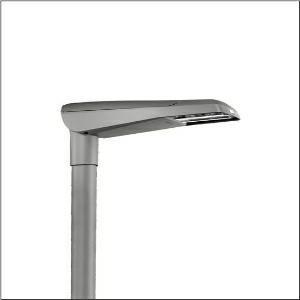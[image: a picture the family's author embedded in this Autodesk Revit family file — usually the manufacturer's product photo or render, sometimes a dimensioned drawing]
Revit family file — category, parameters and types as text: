
# Revit family: streetlight_sl_11_iq_micro___st0_5a_5xc1bc1f08ce_e478
name_source: partatom
category: Lighting Fixtures
units: mm (PartAtom-declared; Revit-internal decimal feet)

## family parameters
Cut with Voids When Loaded = No
Host = Face
Light Source = No
Part Type = Normal
Room Calculation Point = No
Round Connector Dimension = Use Diameter
Shared = No

## types (1)
- --- (1 x LED, 1580 lm, 14 W, 2200K)
    Apparent Load = 14 VA
    CIE Flux Codes = 42 72 97 100 100
    Color Rendering = 70
    Color Temperature = 2200K
    Default Elevation = 1800 mm
    Description = Streetlight SL 11 iQ micro, mast luminaire, primary light control with 3 zone facetted reflector, of plastic, silver coated, highly specular, primary optical cover: cover, of PMMA, transparent, light distribution: ST0.5a, light emission: direct distribution, primary light characteristic: asymmetric, installation type: post-top, side-entry, lamps: LED, High Power LED, rated values: 1.860lm | 13,8W | 134,8lm/W (begin service life); end service life: 1.860lm | 14W; at 50% lumin. flux: 930lm | 7,5W | 124lm/W, colour temperature: 2200/2700/3000/4000K, colour rendering: CRI > 70, light colour: 722/727/730/740, light setting 1 begin service life: 100% | 1.860lm | 13,8W | 134,8lm/W | 3.000K, light setting 1 end service life: 14W, further light settings possible, control: Street-Remote, Auto-Match, Temp-Guard, Lumen-Switch, Night-Set, Smart-Wire, Light-Fading, Desk-Remote (wireless, voltage-free reading and setting of iQ features in the workshop via application-optimized NFC function/RFID function), optimised constant luminous flux control (CLO 2.0), with cable H07RN-F 5x 1.5mm², mains connection: 220..240V, AC, 50/60Hz, connection cable pre-assembled, cable length: 5,5m, luminaire housing, of diecast aluminium, powder-coated, Siteco® metallic grey (DB 702S), please order mast flange separately, inclination adjustable without tools: 0°, 5°, 10°, 15° (post-top) | 0°, -5°, -10°, -15° (side-entry), sealing non-destructively replaceable, multi-level sealing system, length: 600mm, width: 174mm, height: 116mm, mast flange for spigot size: 42mm (side-entry): 5XC10008XM4, 60/48mm (side-entry/post-top): 5XC10108XM2, 76/60mm (side-entry/post-top): 5XC10108XM1, equipment: standard, protection rating (complete): IP66, insulation class (complete): insulation class II (safety insulation), certification: CE, ENEC, ENEC+, VDE, impact resistance: IK10, permissible operating ambient temperature for outdoor applications: -25..+50°C, standard-compliant lighting for roads and squares, Environmental Product Declaration (EPD) tested and certified by an independent institute, packaging unit: 1 piece

Light Distribution: ST0.5a
    Height = 116 mm
    Lamp = 1 x LED
    Lamp Light Flux = 1580 lm
    Lamp Power = 14 W
    Lamp count = 1
    Length = 600 mm
    Luminous efficacy = 113 lm/W
    Manufacturer = Siteco
    ModVariant = No
    Model = 5XC1BC1F08CE
    Number of Poles = 1
    OnlyDefault = Yes
    Power Factor = 1
    Product Name = Streetlight SL 11 iQ micro | ST0.5a
    Product group = mast luminaire | pylon top
    ProductGroupID = 6100
    Protection Class = Protection class II
    Protection Degree = IP 66
    RLX_Detail_Level = 1
    RLX_Emergency_Light_Flux = 0 lm
    RLX_Emergency_Type = 0
    RLX_Emergency_Type_DB = No
    RlxData = <blob elided: 58401 chars, md5=7516babe>
    Socket = socket
    Standby Power = 0 W
    System Light Flux = 1580 lm
    System Power = 14 W
    Type Comments = individual setting: luminous flux: 100 % | dim-lin: 254 | 369 mA
    Type Image = l_1006566.jpg
    URL = http://relux.com
    VarID = @adj_056363
    Voltage = 0 V
    Weight = 0.00 kg
    Width = 174 mm

## geometry (parser evidence)
native form markers: Blend x4, Sweep x12
no freeform markers — native parametric forms only
